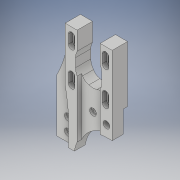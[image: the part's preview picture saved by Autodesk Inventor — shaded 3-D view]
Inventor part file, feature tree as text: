
AUTODESK INVENTOR PART (.ipt)
format: ipt  version: 2018 (Build 220112000, 112)  size: 429,056 bytes
history: native  units: in
note: dims shown in document units (in); Inventor stores cm internally (conversion verified against a paired STEP export)
features: extrude x13, sketch x13, projected_geometry x5, plane x2, fillet x1
ambient origin geometry x8: Origin, YZ Plane, XZ Plane, XY Plane, X Axis, Y Axis, Z Axis, Center Point
bodies: Solid1 (feature_tree)
feature tree (34):
  extrude  "Extrusion1"  Depth=1.6929in
  extrude  "Extrusion2"  Depth=0.4331in
  fillet  "Fillet1"  Radius=1.6535in
  extrude  "Extrusion3"  Depth=1.2205in
  extrude  "Extrusion4"  Depth=0.126in
  extrude  "Extrusion5"  Depth=0.315in
  plane  "Work Plane1"
  plane  "Work Plane2"
  extrude  "Extrusion9"  Depth=0.2362in TaperAngle=0.0deg
  sketch  "Sketch12"  dims[d15=0.315in d16=0.1575in d17=0.0in]
  extrude  "Extrusion13"  Depth=0.1575in TaperAngle=0.0deg
  extrude  "Extrusion14"  Depth=0.2362in
  extrude  "Extrusion15"  Depth=0.9449in
  extrude  "Extrusion16"  Depth=0.315in
  extrude  "Extrusion17"  Depth=0.2165in
  extrude  "Extrusion18"  Depth=0.3937in
  extrude  "Extrusion19"  Depth=0.1575in
  sketch  "Sketch1"  dims[d0=3.8189in d1=1.6929in]
  sketch  "Sketch2"  dims[d2=0.4331in d3=0.4331in d4=1.6535in]
  sketch  "Sketch3"  dims[d5=0.2362in d6=0.0in d7=1.2205in]
  projected_geometry  "Projected Loop1"
  sketch  "Sketch4"  dims[d8=1.2205in d9=0.126in]
  projected_geometry  "Projected Loop2"
  sketch  "Sketch5"  dims[d10=0.2756in d11=0.315in]
  projected_geometry  "Projected Loop3"
  sketch  "Sketch10"  dims[d12=0.315in d13=0.2362in d14=0.0in]
  projected_geometry  "Projected Loop4"
  sketch  "Sketch14"  dims[d18=0.2362in d20=0.2362in]
  sketch  "Sketch15"  dims[d21=0.1575in d22=0.0in d23=0.9449in]
  sketch  "Sketch16"  dims[d24=0.315in d25=0.6102in]
  sketch  "Sketch17"  dims[d26=0.0in d27=0.0in d43=0.2165in]
  sketch  "Sketch18"  dims[d44=0.1654in d47=0.3937in]
  sketch  "Sketch19"  dims[d50=0.2362in d51=0.0in d69=1.2992in d70=4.2606in d71=0.3937in d72=0.0in d73=0.1181in d74=1.063in d75=7.0866in d76=0.3937in d77=0.0in d78=0.2047in d79=0.2441in d80=0.2362in d81=0.0in d82=0.3937in d83=0.1654in d84=0.1654in d85=0.315in d86=0.4724in d87=0.2362in d88=0.0in d89=0.2441in d91=0.0787in d92=0.0in d93=0.7874in d94=0.3937in d95=0.0787in d96=0.0in d97=0.3937in d98=0.1575in d99=0.0in]
  projected_geometry  "Projected Loop5"
